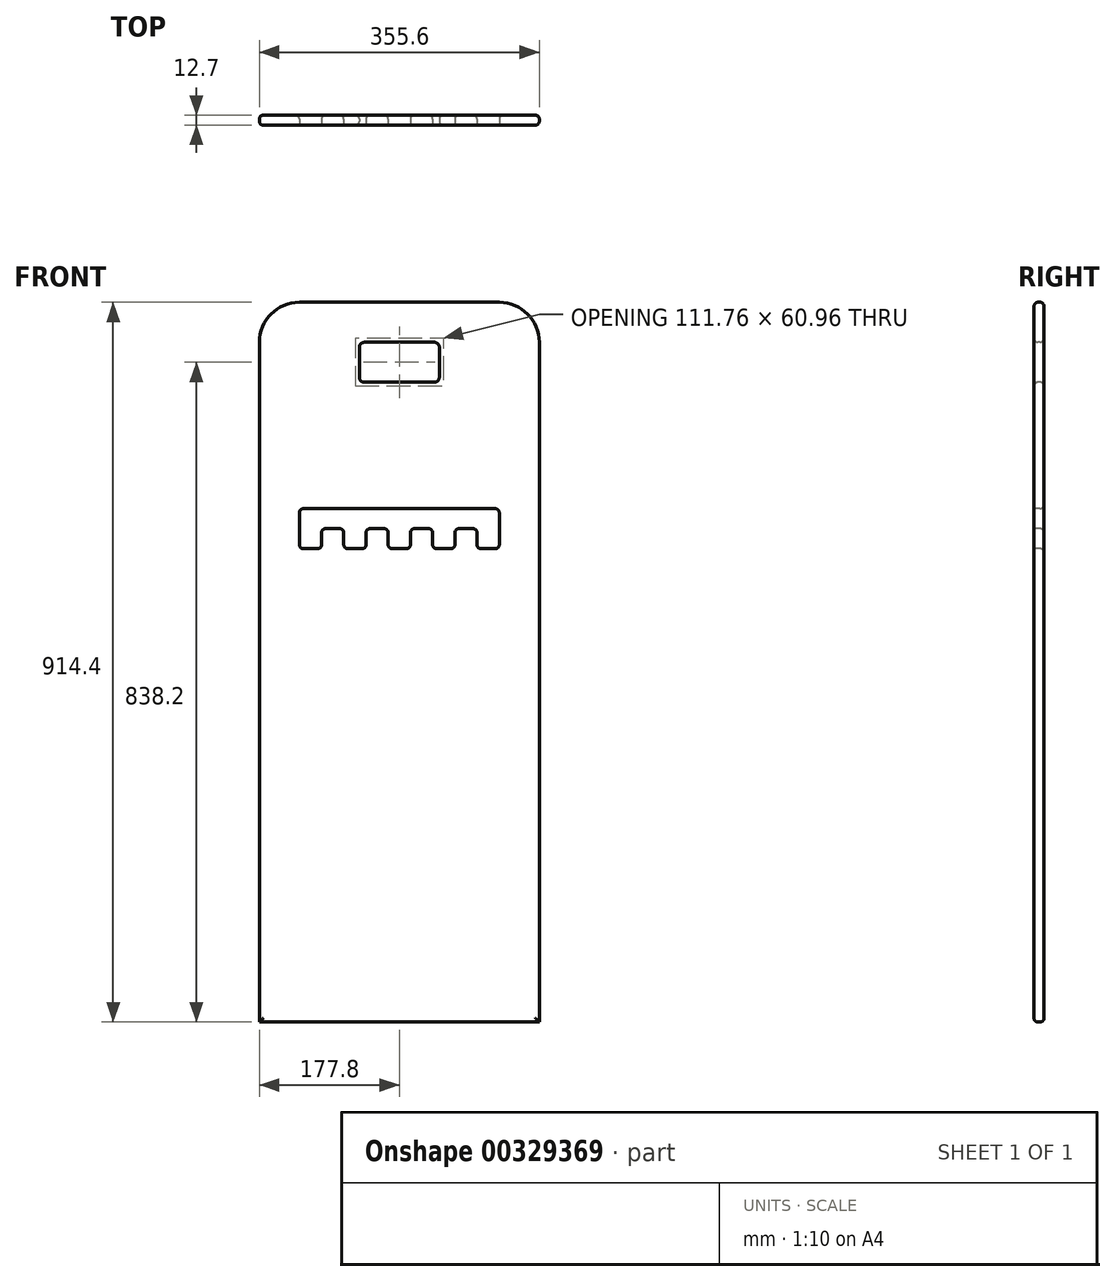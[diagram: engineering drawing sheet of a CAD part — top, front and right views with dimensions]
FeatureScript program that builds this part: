
annotation { "Feature Type Name" : "Feature", "Feature Type Description" : "" }
export const myFeature = defineFeature(function(context is Context, id is Id, definition is map)
    precondition{}
    {
        {
            var Q0;
            Q0=qCreatedBy(makeId("Front.planeOp"),FACE);
            var sketch = newSketch(context, id + "F0", { "sketchPlane" : qUnion([Q0])});
            skLineSegment(sketch, "E0.bottom", {"start": v(127, 457.2) * mm, "end": v(-127, 457.2) * mm});
            skLineSegment(sketch, "E0.top", {"start": v(177.8, -457.2) * mm, "end": v(-177.8, -457.2) * mm});
            skLineSegment(sketch, "E0.left", {"start": v(177.8, 406.4) * mm, "end": v(177.8, -457.2) * mm});
            skLineSegment(sketch, "E0.right", {"start": v(-177.8, 406.4) * mm, "end": v(-177.8, -457.2) * mm});
            skPoint(sketch, "E0.middle", {"position": v(0, 0) * mm});
            skPoint(sketch, "E1.visualSharp", {"position": v(-177.8, 457.2) * mm});
            skArc(sketch, "E1.filletArc", {"start": v(-127, 457.2) * mm, "mid": v(-162.92, 442.32) * mm, "end": v(-177.8, 406.4) * mm});
            skPoint(sketch, "E2.visualSharp", {"position": v(177.8, 457.2) * mm});
            skArc(sketch, "E2.filletArc", {"start": v(177.8, 406.4) * mm, "mid": v(162.92, 442.32) * mm, "end": v(127, 457.2) * mm});
            skSolve(sketch);
        }
        {
            var Q0;
            Q0 = qSketchRegion(id + "F0", true);
            extrude(context, id + "F1", {"entities" : qUnion([Q0]), "depth" : 12.7 * mm});
        }
        {
            var Q0;
            Q0=makeQuery(id+"F1.opExtrude","CAP_FACE",FACE,{"disambiguationData":[OSD([sQuery(id+"F0.wireOp",EDGE,"E0.bottom"),sQuery(id+"F0.wireOp",EDGE,"E0.top"),sQuery(id+"F0.wireOp",EDGE,"E0.left"),sQuery(id+"F0.wireOp",EDGE,"E0.right")])],"isStart":false});
            var sketch = newSketch(context, id + "F2", { "sketchPlane" : qUnion([Q0])});
            skLineSegment(sketch, "E3", {"start": v(0, 457.2) * mm, "end": v(127, 457.2) * mm, "construction": true});
            skLineSegment(sketch, "E4", {"start": v(0, 457.2) * mm, "end": v(0, 406.4) * mm, "construction": true});
            skLineSegment(sketch, "E5", {"start": v(0, 406.4) * mm, "end": v(-44.45, 406.4) * mm});
            skLineSegment(sketch, "E6", {"start": v(-50.8, 400.05) * mm, "end": v(-50.8, 361.95) * mm});
            skLineSegment(sketch, "E7", {"start": v(-44.45, 355.6) * mm, "end": v(44.45, 355.6) * mm});
            skLineSegment(sketch, "E8", {"start": v(50.8, 361.95) * mm, "end": v(50.8, 400.05) * mm});
            skLineSegment(sketch, "E9", {"start": v(44.45, 406.4) * mm, "end": v(0, 406.4) * mm});
            skPoint(sketch, "E10.visualSharp", {"position": v(-50.8, 406.4) * mm});
            skArc(sketch, "E10.filletArc", {"start": v(-44.45, 406.4) * mm, "mid": v(-48.94, 404.54) * mm, "end": v(-50.8, 400.05) * mm});
            skPoint(sketch, "E11.visualSharp", {"position": v(-50.8, 355.6) * mm});
            skArc(sketch, "E11.filletArc", {"start": v(-50.8, 361.95) * mm, "mid": v(-48.94, 357.46) * mm, "end": v(-44.45, 355.6) * mm});
            skPoint(sketch, "E12.visualSharp", {"position": v(50.8, 355.6) * mm});
            skArc(sketch, "E12.filletArc", {"start": v(44.45, 355.6) * mm, "mid": v(48.94, 357.46) * mm, "end": v(50.8, 361.95) * mm});
            skPoint(sketch, "E13.visualSharp", {"position": v(50.8, 406.4) * mm});
            skArc(sketch, "E13.filletArc", {"start": v(50.8, 400.05) * mm, "mid": v(48.94, 404.54) * mm, "end": v(44.45, 406.4) * mm});
            skSolve(sketch);
        }
        {
            var Q0;
            Q0=makeQuery(id+"F2.imprint","IMPRINT",FACE,{"disambiguationData":[TD([[makeQuery(id+"F2.imprint","IMPRINT",EDGE,{"derivedFrom":sQuery(id+"F2.wireOp",EDGE,"E5")}),1.0]])]});
            extrude(context, id + "F3", {"entities" : qUnion([Q0]), "operationType" : NewBodyOperationType.REMOVE, "oppositeDirection" : true, "depth" : 25.4 * mm});
        }
        {
            var Q0;
            Q0=makeQuery(id+"F1.opExtrude","CAP_FACE",FACE,{"disambiguationData":[OSD([sQuery(id+"F0.wireOp",EDGE,"E0.bottom"),sQuery(id+"F0.wireOp",EDGE,"E0.top"),sQuery(id+"F0.wireOp",EDGE,"E0.left"),sQuery(id+"F0.wireOp",EDGE,"E0.right"),sQuery(id+"F0.wireOp",EDGE,"E1.filletArc"),sQuery(id+"F0.wireOp",EDGE,"E2.filletArc")])],"isStart":false});
            fillet(context, id + "F4", {"entities" : qUnion([Q0]), "radius" : 5.08 * mm, "tangentPropagation" : true, "allowEdgeOverflow" : false});
        }
        {
            var Q0;
            Q0=makeQuery(id+"F1.opExtrude","CAP_FACE",FACE,{"disambiguationData":[OSD([sQuery(id+"F0.wireOp",EDGE,"E0.bottom"),sQuery(id+"F0.wireOp",EDGE,"E0.top"),sQuery(id+"F0.wireOp",EDGE,"E0.left"),sQuery(id+"F0.wireOp",EDGE,"E0.right"),sQuery(id+"F0.wireOp",EDGE,"E1.filletArc"),sQuery(id+"F0.wireOp",EDGE,"E2.filletArc")])],"isStart":true});
            fillet(context, id + "F5", {"entities" : qUnion([Q0]), "radius" : 5.08 * mm, "tangentPropagation" : true, "allowEdgeOverflow" : false});
        }
        {
            var Q0;
            Q0=makeQuery(id+"F1.opExtrude","CAP_FACE",FACE,{"disambiguationData":[OSD([sQuery(id+"F0.wireOp",EDGE,"E0.bottom"),sQuery(id+"F0.wireOp",EDGE,"E0.top"),sQuery(id+"F0.wireOp",EDGE,"E0.left"),sQuery(id+"F0.wireOp",EDGE,"E0.right"),sQuery(id+"F0.wireOp",EDGE,"E1.filletArc"),sQuery(id+"F0.wireOp",EDGE,"E2.filletArc")])],"isStart":false});
            var sketch = newSketch(context, id + "F6", { "sketchPlane" : qUnion([Q0])});
            skLineSegment(sketch, "E14", {"start": v(0, 452.12) * mm, "end": v(0, 194.94) * mm, "construction": true});
            skPoint(sketch, "E14.endSnap0", {"position": v(0, 452.12) * mm});
            skLineSegment(sketch, "E15", {"start": v(0, 194.94) * mm, "end": v(-127, 194.94) * mm});
            skLineSegment(sketch, "E16", {"start": v(-127, 194.94) * mm, "end": v(-127, 144.14) * mm});
            skLineSegment(sketch, "E17", {"start": v(-127, 144.14) * mm, "end": v(127, 144.14) * mm});
            skLineSegment(sketch, "E18", {"start": v(127, 144.14) * mm, "end": v(127, 194.94) * mm});
            skLineSegment(sketch, "E19", {"start": v(127, 194.94) * mm, "end": v(0, 194.94) * mm});
            skLineSegment(sketch, "E20", {"start": v(-127, 144.14) * mm, "end": v(-98.78, 144.14) * mm, "construction": true});
            skLineSegment(sketch, "E21", {"start": v(-98.78, 144.14) * mm, "end": v(-70.56, 144.14) * mm, "construction": true});
            skLineSegment(sketch, "E22", {"start": v(-70.56, 144.14) * mm, "end": v(-42.33, 144.14) * mm, "construction": true});
            skLineSegment(sketch, "E23", {"start": v(-42.33, 144.14) * mm, "end": v(-14.11, 144.14) * mm, "construction": true});
            skLineSegment(sketch, "E24", {"start": v(-14.11, 144.14) * mm, "end": v(14.11, 144.14) * mm, "construction": true});
            skLineSegment(sketch, "E25", {"start": v(14.11, 144.14) * mm, "end": v(42.33, 144.14) * mm, "construction": true});
            skLineSegment(sketch, "E26", {"start": v(42.33, 144.14) * mm, "end": v(70.56, 144.14) * mm, "construction": true});
            skLineSegment(sketch, "E27", {"start": v(70.56, 144.14) * mm, "end": v(98.78, 144.14) * mm, "construction": true});
            skLineSegment(sketch, "E28", {"start": v(98.78, 144.14) * mm, "end": v(98.78, 169.54) * mm});
            skPoint(sketch, "E28.endSnap0", {"position": v(127, 169.54) * mm});
            skLineSegment(sketch, "E29", {"start": v(98.78, 169.54) * mm, "end": v(70.56, 169.54) * mm});
            skLineSegment(sketch, "E30", {"start": v(70.56, 169.54) * mm, "end": v(70.56, 144.14) * mm});
            skLineSegment(sketch, "E31", {"start": v(-98.78, 144.14) * mm, "end": v(-98.78, 169.54) * mm});
            skLineSegment(sketch, "E32", {"start": v(-98.78, 169.54) * mm, "end": v(-70.56, 169.54) * mm});
            skLineSegment(sketch, "E33", {"start": v(-70.56, 169.54) * mm, "end": v(-70.56, 144.14) * mm});
            skLineSegment(sketch, "E34", {"start": v(-42.33, 144.14) * mm, "end": v(-42.33, 169.54) * mm});
            skLineSegment(sketch, "E35", {"start": v(-42.33, 169.54) * mm, "end": v(-14.11, 169.54) * mm});
            skLineSegment(sketch, "E36", {"start": v(-14.11, 169.54) * mm, "end": v(-14.11, 144.14) * mm});
            skLineSegment(sketch, "E37", {"start": v(14.11, 144.14) * mm, "end": v(14.11, 169.54) * mm});
            skLineSegment(sketch, "E38", {"start": v(14.11, 169.54) * mm, "end": v(42.33, 169.54) * mm});
            skLineSegment(sketch, "E39", {"start": v(42.33, 144.14) * mm, "end": v(42.33, 169.54) * mm});
            skSolve(sketch);
        }
        {
            var Q0;
            Q0=makeQuery(id+"F6.imprint","IMPRINT",FACE,{"disambiguationData":[TD([[makeQuery(id+"F6.imprint","IMPRINT",EDGE,{"derivedFrom":sQuery(id+"F6.wireOp",EDGE,"E15")}),1.0]])]});
            extrude(context, id + "F7", {"entities" : qUnion([Q0]), "operationType" : NewBodyOperationType.REMOVE, "oppositeDirection" : true, "depth" : 25.4 * mm});
        }
        {
            var Q0;
            Q0=makeQuery(id+"F7.boolean.opBoolean","COPY",EDGE,{"derivedFrom":makeQuery(id+"F7.opExtrude","CAP_EDGE",EDGE,{"disambiguationData":[OSD([sQuery(id+"F6.wireOp",EDGE,"E31")])],"isStart":true})});
            var Q1;
            Q1=makeQuery(id+"F7.boolean.opBoolean","COPY",EDGE,{"derivedFrom":makeQuery(id+"F7.opExtrude","CAP_EDGE",EDGE,{"disambiguationData":[OSD([sQuery(id+"F6.wireOp",EDGE,"E32")])],"isStart":true})});
            var Q2;
            Q2=makeQuery(id+"F7.boolean.opBoolean","COPY",EDGE,{"derivedFrom":makeQuery(id+"F7.opExtrude","CAP_EDGE",EDGE,{"disambiguationData":[OSD([sQuery(id+"F6.wireOp",EDGE,"E33")])],"isStart":true})});
            var Q3;
            Q3=makeQuery(id+"F7.boolean.opBoolean","COPY",EDGE,{"derivedFrom":makeQuery(id+"F7.opExtrude","CAP_EDGE",EDGE,{"disambiguationData":[OSD([sQuery(id+"F6.wireOp",EDGE,"E34")])],"isStart":true})});
            var Q4;
            Q4=makeQuery(id+"F7.boolean.opBoolean","COPY",EDGE,{"derivedFrom":makeQuery(id+"F7.opExtrude","CAP_EDGE",EDGE,{"disambiguationData":[OSD([sQuery(id+"F6.wireOp",EDGE,"E35")])],"isStart":true})});
            var Q5;
            Q5=makeQuery(id+"F7.boolean.opBoolean","COPY",EDGE,{"derivedFrom":makeQuery(id+"F7.opExtrude","CAP_EDGE",EDGE,{"disambiguationData":[OSD([sQuery(id+"F6.wireOp",EDGE,"E15"),sQuery(id+"F6.wireOp",EDGE,"E19")])],"isStart":true})});
            var Q6;
            Q6=makeQuery(id+"F7.boolean.opBoolean","COPY",EDGE,{"derivedFrom":makeQuery(id+"F7.opExtrude","CAP_EDGE",EDGE,{"disambiguationData":[OSD([sQuery(id+"F6.wireOp",EDGE,"E36")])],"isStart":true})});
            var Q7;
            Q7=makeQuery(id+"F7.boolean.opBoolean","COPY",EDGE,{"derivedFrom":makeQuery(id+"F7.opExtrude","CAP_EDGE",EDGE,{"disambiguationData":[OSD([sQuery(id+"F6.wireOp",EDGE,"E16")])],"isStart":true})});
            var Q8;
            Q8=makeQuery(id+"F7.boolean.opBoolean","COPY",EDGE,{"derivedFrom":makeQuery(id+"F7.opExtrude","CAP_EDGE",EDGE,{"disambiguationData":[OSD([sQuery(id+"F6.wireOp",EDGE,"E37")])],"isStart":true})});
            var Q9;
            {var subQ0=sQuery(id+"F6.wireOp",EDGE,"E17");Q9=makeQuery(id+"F7.boolean.opBoolean","COPY",EDGE,{"derivedFrom":makeQuery(id+"F7.opExtrude","CAP_EDGE",EDGE,{"disambiguationData":[OSD([subQ0]),TDD([makeQuery(id+"F6.imprint","IMPRINT",EDGE,{"disambiguationData":[TD([[makeQuery(id+"F6.imprint","INTERSECT",VERTEX,{"derivedFrom":[sQuery(id+"F6.wireOp",EDGE,"E16"),subQ0]}),-1.0]])],"derivedFrom":subQ0})])],"isStart":true})});}
            var Q10;
            Q10=makeQuery(id+"F7.boolean.opBoolean","COPY",EDGE,{"derivedFrom":makeQuery(id+"F7.opExtrude","CAP_EDGE",EDGE,{"disambiguationData":[OSD([sQuery(id+"F6.wireOp",EDGE,"E38")])],"isStart":true})});
            var Q11;
            {var subQ0=sQuery(id+"F6.wireOp",EDGE,"E17");Q11=makeQuery(id+"F7.boolean.opBoolean","COPY",EDGE,{"derivedFrom":makeQuery(id+"F7.opExtrude","CAP_EDGE",EDGE,{"disambiguationData":[OSD([subQ0]),TDD([makeQuery(id+"F6.imprint","IMPRINT",EDGE,{"disambiguationData":[TD([[makeQuery(id+"F6.imprint","INTERSECT",VERTEX,{"derivedFrom":[subQ0,sQuery(id+"F6.wireOp",EDGE,"E33")]}),-1.0]])],"derivedFrom":subQ0})])],"isStart":true})});}
            var Q12;
            {var subQ0=sQuery(id+"F6.wireOp",EDGE,"E17");Q12=makeQuery(id+"F7.boolean.opBoolean","COPY",EDGE,{"derivedFrom":makeQuery(id+"F7.opExtrude","CAP_EDGE",EDGE,{"disambiguationData":[OSD([subQ0]),TDD([makeQuery(id+"F6.imprint","IMPRINT",EDGE,{"disambiguationData":[TD([[makeQuery(id+"F6.imprint","INTERSECT",VERTEX,{"derivedFrom":[subQ0,sQuery(id+"F6.wireOp",EDGE,"E36")]}),-1.0]])],"derivedFrom":subQ0})])],"isStart":true})});}
            var Q13;
            {var subQ0=sQuery(id+"F6.wireOp",EDGE,"E17");Q13=makeQuery(id+"F7.boolean.opBoolean","COPY",EDGE,{"derivedFrom":makeQuery(id+"F7.opExtrude","CAP_EDGE",EDGE,{"disambiguationData":[OSD([subQ0]),TDD([makeQuery(id+"F6.imprint","IMPRINT",EDGE,{"disambiguationData":[TD([[makeQuery(id+"F6.imprint","INTERSECT",VERTEX,{"derivedFrom":[subQ0,sQuery(id+"F6.wireOp",EDGE,"E30")]}),1.0]])],"derivedFrom":subQ0})])],"isStart":true})});}
            var Q14;
            {var subQ0=sQuery(id+"F6.wireOp",EDGE,"E17");Q14=makeQuery(id+"F7.boolean.opBoolean","COPY",EDGE,{"derivedFrom":makeQuery(id+"F7.opExtrude","CAP_EDGE",EDGE,{"disambiguationData":[OSD([subQ0]),TDD([makeQuery(id+"F6.imprint","IMPRINT",EDGE,{"disambiguationData":[TD([[makeQuery(id+"F6.imprint","INTERSECT",VERTEX,{"derivedFrom":[subQ0,sQuery(id+"F6.wireOp",EDGE,"E18")]}),1.0]])],"derivedFrom":subQ0})])],"isStart":true})});}
            var Q15;
            Q15=makeQuery(id+"F7.boolean.opBoolean","COPY",EDGE,{"derivedFrom":makeQuery(id+"F7.opExtrude","CAP_EDGE",EDGE,{"disambiguationData":[OSD([sQuery(id+"F6.wireOp",EDGE,"E18")])],"isStart":true})});
            var Q16;
            Q16=makeQuery(id+"F7.boolean.opBoolean","COPY",EDGE,{"derivedFrom":makeQuery(id+"F7.opExtrude","SWEPT_EDGE",EDGE,{"disambiguationData":[OSD([sQuery(id+"F6.wireOp",EDGE,"E34"),sQuery(id+"F6.wireOp",EDGE,"E35")])]})});
            var Q17;
            Q17=makeQuery(id+"F7.boolean.opBoolean","COPY",EDGE,{"derivedFrom":makeQuery(id+"F7.opExtrude","SWEPT_EDGE",EDGE,{"disambiguationData":[OSD([sQuery(id+"F6.wireOp",EDGE,"E15"),sQuery(id+"F6.wireOp",EDGE,"E16")])]})});
            var Q18;
            Q18=makeQuery(id+"F7.boolean.opBoolean","COPY",EDGE,{"derivedFrom":makeQuery(id+"F7.opExtrude","SWEPT_EDGE",EDGE,{"disambiguationData":[OSD([sQuery(id+"F6.wireOp",EDGE,"E16"),sQuery(id+"F6.wireOp",EDGE,"E17")])]})});
            var Q19;
            Q19=makeQuery(id+"F7.boolean.opBoolean","COPY",EDGE,{"derivedFrom":makeQuery(id+"F7.opExtrude","SWEPT_EDGE",EDGE,{"disambiguationData":[OSD([sQuery(id+"F6.wireOp",EDGE,"E17"),sQuery(id+"F6.wireOp",EDGE,"E28")])]})});
            var Q20;
            Q20=makeQuery(id+"F7.boolean.opBoolean","COPY",EDGE,{"derivedFrom":makeQuery(id+"F7.opExtrude","SWEPT_EDGE",EDGE,{"disambiguationData":[OSD([sQuery(id+"F6.wireOp",EDGE,"E28"),sQuery(id+"F6.wireOp",EDGE,"E29")])]})});
            var Q21;
            Q21=makeQuery(id+"F7.boolean.opBoolean","COPY",EDGE,{"derivedFrom":makeQuery(id+"F7.opExtrude","SWEPT_EDGE",EDGE,{"disambiguationData":[OSD([sQuery(id+"F6.wireOp",EDGE,"E29"),sQuery(id+"F6.wireOp",EDGE,"E30")])]})});
            var Q22;
            Q22=makeQuery(id+"F7.boolean.opBoolean","COPY",EDGE,{"derivedFrom":makeQuery(id+"F7.opExtrude","SWEPT_EDGE",EDGE,{"disambiguationData":[OSD([sQuery(id+"F6.wireOp",EDGE,"E17"),sQuery(id+"F6.wireOp",EDGE,"E30")])]})});
            var Q23;
            Q23=makeQuery(id+"F7.boolean.opBoolean","COPY",EDGE,{"derivedFrom":makeQuery(id+"F7.opExtrude","SWEPT_EDGE",EDGE,{"disambiguationData":[OSD([sQuery(id+"F6.wireOp",EDGE,"E17"),sQuery(id+"F6.wireOp",EDGE,"E31")])]})});
            var Q24;
            Q24=makeQuery(id+"F7.boolean.opBoolean","COPY",EDGE,{"derivedFrom":makeQuery(id+"F7.opExtrude","CAP_EDGE",EDGE,{"disambiguationData":[OSD([sQuery(id+"F6.wireOp",EDGE,"E29")])],"isStart":true})});
            var Q25;
            {var subQ0=sQuery(id+"F6.wireOp",EDGE,"E17");Q25=makeQuery(id+"F7.boolean.opBoolean","INTERSECT",EDGE,{"derivedFrom":[makeQuery(id+"F1.opExtrude","CAP_FACE",FACE,{"disambiguationData":[OSD([sQuery(id+"F0.wireOp",EDGE,"E0.bottom"),sQuery(id+"F0.wireOp",EDGE,"E0.top"),sQuery(id+"F0.wireOp",EDGE,"E0.left"),sQuery(id+"F0.wireOp",EDGE,"E0.right"),sQuery(id+"F0.wireOp",EDGE,"E1.filletArc"),sQuery(id+"F0.wireOp",EDGE,"E2.filletArc")])],"isStart":true}),makeQuery(id+"F7.opExtrude","SWEPT_FACE",FACE,{"disambiguationData":[OSD([subQ0]),TDD([makeQuery(id+"F6.imprint","IMPRINT",EDGE,{"disambiguationData":[TD([[makeQuery(id+"F6.imprint","INTERSECT",VERTEX,{"derivedFrom":[subQ0,sQuery(id+"F6.wireOp",EDGE,"E30")]}),1.0]])],"derivedFrom":subQ0})])]})]});}
            var Q26;
            Q26=makeQuery(id+"F7.boolean.opBoolean","COPY",EDGE,{"derivedFrom":makeQuery(id+"F7.opExtrude","CAP_EDGE",EDGE,{"disambiguationData":[OSD([sQuery(id+"F6.wireOp",EDGE,"E30")])],"isStart":true})});
            var Q27;
            {var subQ0=sQuery(id+"F6.wireOp",EDGE,"E17");Q27=makeQuery(id+"F7.boolean.opBoolean","INTERSECT",EDGE,{"derivedFrom":[makeQuery(id+"F1.opExtrude","CAP_FACE",FACE,{"disambiguationData":[OSD([sQuery(id+"F0.wireOp",EDGE,"E0.bottom"),sQuery(id+"F0.wireOp",EDGE,"E0.top"),sQuery(id+"F0.wireOp",EDGE,"E0.left"),sQuery(id+"F0.wireOp",EDGE,"E0.right"),sQuery(id+"F0.wireOp",EDGE,"E1.filletArc"),sQuery(id+"F0.wireOp",EDGE,"E2.filletArc")])],"isStart":true}),makeQuery(id+"F7.opExtrude","SWEPT_FACE",FACE,{"disambiguationData":[OSD([subQ0]),TDD([makeQuery(id+"F6.imprint","IMPRINT",EDGE,{"disambiguationData":[TD([[makeQuery(id+"F6.imprint","INTERSECT",VERTEX,{"derivedFrom":[subQ0,sQuery(id+"F6.wireOp",EDGE,"E18")]}),1.0]])],"derivedFrom":subQ0})])]})]});}
            var Q28;
            Q28=makeQuery(id+"F7.boolean.opBoolean","COPY",EDGE,{"derivedFrom":makeQuery(id+"F7.opExtrude","SWEPT_EDGE",EDGE,{"disambiguationData":[OSD([sQuery(id+"F6.wireOp",EDGE,"E17"),sQuery(id+"F6.wireOp",EDGE,"E37")])]})});
            var Q29;
            Q29=makeQuery(id+"F7.boolean.opBoolean","COPY",EDGE,{"derivedFrom":makeQuery(id+"F7.opExtrude","SWEPT_EDGE",EDGE,{"disambiguationData":[OSD([sQuery(id+"F6.wireOp",EDGE,"E17"),sQuery(id+"F6.wireOp",EDGE,"E39")])]})});
            var Q30;
            Q30=makeQuery(id+"F7.boolean.opBoolean","INTERSECT",EDGE,{"derivedFrom":[makeQuery(id+"F1.opExtrude","CAP_FACE",FACE,{"disambiguationData":[OSD([sQuery(id+"F0.wireOp",EDGE,"E0.bottom"),sQuery(id+"F0.wireOp",EDGE,"E0.top"),sQuery(id+"F0.wireOp",EDGE,"E0.left"),sQuery(id+"F0.wireOp",EDGE,"E0.right"),sQuery(id+"F0.wireOp",EDGE,"E1.filletArc"),sQuery(id+"F0.wireOp",EDGE,"E2.filletArc")])],"isStart":true}),makeQuery(id+"F7.opExtrude","SWEPT_FACE",FACE,{"disambiguationData":[OSD([sQuery(id+"F6.wireOp",EDGE,"E31")])]})]});
            var Q31;
            Q31=makeQuery(id+"F7.boolean.opBoolean","INTERSECT",EDGE,{"derivedFrom":[makeQuery(id+"F1.opExtrude","CAP_FACE",FACE,{"disambiguationData":[OSD([sQuery(id+"F0.wireOp",EDGE,"E0.bottom"),sQuery(id+"F0.wireOp",EDGE,"E0.top"),sQuery(id+"F0.wireOp",EDGE,"E0.left"),sQuery(id+"F0.wireOp",EDGE,"E0.right"),sQuery(id+"F0.wireOp",EDGE,"E1.filletArc"),sQuery(id+"F0.wireOp",EDGE,"E2.filletArc")])],"isStart":true}),makeQuery(id+"F7.opExtrude","SWEPT_FACE",FACE,{"disambiguationData":[OSD([sQuery(id+"F6.wireOp",EDGE,"E33")])]})]});
            var Q32;
            Q32=makeQuery(id+"F7.boolean.opBoolean","INTERSECT",EDGE,{"derivedFrom":[makeQuery(id+"F1.opExtrude","CAP_FACE",FACE,{"disambiguationData":[OSD([sQuery(id+"F0.wireOp",EDGE,"E0.bottom"),sQuery(id+"F0.wireOp",EDGE,"E0.top"),sQuery(id+"F0.wireOp",EDGE,"E0.left"),sQuery(id+"F0.wireOp",EDGE,"E0.right"),sQuery(id+"F0.wireOp",EDGE,"E1.filletArc"),sQuery(id+"F0.wireOp",EDGE,"E2.filletArc")])],"isStart":true}),makeQuery(id+"F7.opExtrude","SWEPT_FACE",FACE,{"disambiguationData":[OSD([sQuery(id+"F6.wireOp",EDGE,"E34")])]})]});
            var Q33;
            Q33=makeQuery(id+"F7.boolean.opBoolean","COPY",EDGE,{"derivedFrom":makeQuery(id+"F7.opExtrude","CAP_EDGE",EDGE,{"disambiguationData":[OSD([sQuery(id+"F6.wireOp",EDGE,"E39")])],"isStart":true})});
            var Q34;
            Q34=makeQuery(id+"F7.boolean.opBoolean","INTERSECT",EDGE,{"derivedFrom":[makeQuery(id+"F1.opExtrude","CAP_FACE",FACE,{"disambiguationData":[OSD([sQuery(id+"F0.wireOp",EDGE,"E0.bottom"),sQuery(id+"F0.wireOp",EDGE,"E0.top"),sQuery(id+"F0.wireOp",EDGE,"E0.left"),sQuery(id+"F0.wireOp",EDGE,"E0.right"),sQuery(id+"F0.wireOp",EDGE,"E1.filletArc"),sQuery(id+"F0.wireOp",EDGE,"E2.filletArc")])],"isStart":true}),makeQuery(id+"F7.opExtrude","SWEPT_FACE",FACE,{"disambiguationData":[OSD([sQuery(id+"F6.wireOp",EDGE,"E35")])]})]});
            var Q35;
            Q35=makeQuery(id+"F7.boolean.opBoolean","INTERSECT",EDGE,{"derivedFrom":[makeQuery(id+"F1.opExtrude","CAP_FACE",FACE,{"disambiguationData":[OSD([sQuery(id+"F0.wireOp",EDGE,"E0.bottom"),sQuery(id+"F0.wireOp",EDGE,"E0.top"),sQuery(id+"F0.wireOp",EDGE,"E0.left"),sQuery(id+"F0.wireOp",EDGE,"E0.right"),sQuery(id+"F0.wireOp",EDGE,"E1.filletArc"),sQuery(id+"F0.wireOp",EDGE,"E2.filletArc")])],"isStart":true}),makeQuery(id+"F7.opExtrude","SWEPT_FACE",FACE,{"disambiguationData":[OSD([sQuery(id+"F6.wireOp",EDGE,"E15"),sQuery(id+"F6.wireOp",EDGE,"E19")])]})]});
            var Q36;
            Q36=makeQuery(id+"F7.boolean.opBoolean","INTERSECT",EDGE,{"derivedFrom":[makeQuery(id+"F1.opExtrude","CAP_FACE",FACE,{"disambiguationData":[OSD([sQuery(id+"F0.wireOp",EDGE,"E0.bottom"),sQuery(id+"F0.wireOp",EDGE,"E0.top"),sQuery(id+"F0.wireOp",EDGE,"E0.left"),sQuery(id+"F0.wireOp",EDGE,"E0.right"),sQuery(id+"F0.wireOp",EDGE,"E1.filletArc"),sQuery(id+"F0.wireOp",EDGE,"E2.filletArc")])],"isStart":true}),makeQuery(id+"F7.opExtrude","SWEPT_FACE",FACE,{"disambiguationData":[OSD([sQuery(id+"F6.wireOp",EDGE,"E16")])]})]});
            var Q37;
            Q37=makeQuery(id+"F7.boolean.opBoolean","INTERSECT",EDGE,{"derivedFrom":[makeQuery(id+"F1.opExtrude","CAP_FACE",FACE,{"disambiguationData":[OSD([sQuery(id+"F0.wireOp",EDGE,"E0.bottom"),sQuery(id+"F0.wireOp",EDGE,"E0.top"),sQuery(id+"F0.wireOp",EDGE,"E0.left"),sQuery(id+"F0.wireOp",EDGE,"E0.right"),sQuery(id+"F0.wireOp",EDGE,"E1.filletArc"),sQuery(id+"F0.wireOp",EDGE,"E2.filletArc")])],"isStart":true}),makeQuery(id+"F7.opExtrude","SWEPT_FACE",FACE,{"disambiguationData":[OSD([sQuery(id+"F6.wireOp",EDGE,"E37")])]})]});
            var Q38;
            {var subQ0=sQuery(id+"F6.wireOp",EDGE,"E17");Q38=makeQuery(id+"F7.boolean.opBoolean","INTERSECT",EDGE,{"derivedFrom":[makeQuery(id+"F1.opExtrude","CAP_FACE",FACE,{"disambiguationData":[OSD([sQuery(id+"F0.wireOp",EDGE,"E0.bottom"),sQuery(id+"F0.wireOp",EDGE,"E0.top"),sQuery(id+"F0.wireOp",EDGE,"E0.left"),sQuery(id+"F0.wireOp",EDGE,"E0.right"),sQuery(id+"F0.wireOp",EDGE,"E1.filletArc"),sQuery(id+"F0.wireOp",EDGE,"E2.filletArc")])],"isStart":true}),makeQuery(id+"F7.opExtrude","SWEPT_FACE",FACE,{"disambiguationData":[OSD([subQ0]),TDD([makeQuery(id+"F6.imprint","IMPRINT",EDGE,{"disambiguationData":[TD([[makeQuery(id+"F6.imprint","INTERSECT",VERTEX,{"derivedFrom":[sQuery(id+"F6.wireOp",EDGE,"E16"),subQ0]}),-1.0]])],"derivedFrom":subQ0})])]})]});}
            var Q39;
            Q39=makeQuery(id+"F7.boolean.opBoolean","COPY",EDGE,{"derivedFrom":makeQuery(id+"F7.opExtrude","CAP_EDGE",EDGE,{"disambiguationData":[OSD([sQuery(id+"F6.wireOp",EDGE,"E28")])],"isStart":true})});
            var Q40;
            {var subQ0=sQuery(id+"F6.wireOp",EDGE,"E17");Q40=makeQuery(id+"F7.boolean.opBoolean","INTERSECT",EDGE,{"derivedFrom":[makeQuery(id+"F1.opExtrude","CAP_FACE",FACE,{"disambiguationData":[OSD([sQuery(id+"F0.wireOp",EDGE,"E0.bottom"),sQuery(id+"F0.wireOp",EDGE,"E0.top"),sQuery(id+"F0.wireOp",EDGE,"E0.left"),sQuery(id+"F0.wireOp",EDGE,"E0.right"),sQuery(id+"F0.wireOp",EDGE,"E1.filletArc"),sQuery(id+"F0.wireOp",EDGE,"E2.filletArc")])],"isStart":true}),makeQuery(id+"F7.opExtrude","SWEPT_FACE",FACE,{"disambiguationData":[OSD([subQ0]),TDD([makeQuery(id+"F6.imprint","IMPRINT",EDGE,{"disambiguationData":[TD([[makeQuery(id+"F6.imprint","INTERSECT",VERTEX,{"derivedFrom":[subQ0,sQuery(id+"F6.wireOp",EDGE,"E36")]}),-1.0]])],"derivedFrom":subQ0})])]})]});}
            var Q41;
            Q41=makeQuery(id+"F7.boolean.opBoolean","COPY",EDGE,{"derivedFrom":makeQuery(id+"F7.opExtrude","SWEPT_EDGE",EDGE,{"disambiguationData":[OSD([sQuery(id+"F6.wireOp",EDGE,"E35"),sQuery(id+"F6.wireOp",EDGE,"E36")])]})});
            var Q42;
            Q42=makeQuery(id+"F7.boolean.opBoolean","COPY",EDGE,{"derivedFrom":makeQuery(id+"F7.opExtrude","SWEPT_EDGE",EDGE,{"disambiguationData":[OSD([sQuery(id+"F6.wireOp",EDGE,"E17"),sQuery(id+"F6.wireOp",EDGE,"E36")])]})});
            var Q43;
            Q43=makeQuery(id+"F7.boolean.opBoolean","COPY",EDGE,{"derivedFrom":makeQuery(id+"F7.opExtrude","SWEPT_EDGE",EDGE,{"disambiguationData":[OSD([sQuery(id+"F6.wireOp",EDGE,"E17"),sQuery(id+"F6.wireOp",EDGE,"E18")])]})});
            var Q44;
            Q44=makeQuery(id+"F7.boolean.opBoolean","COPY",EDGE,{"derivedFrom":makeQuery(id+"F7.opExtrude","SWEPT_EDGE",EDGE,{"disambiguationData":[OSD([sQuery(id+"F6.wireOp",EDGE,"E18"),sQuery(id+"F6.wireOp",EDGE,"E19")])]})});
            var Q45;
            Q45=makeQuery(id+"F7.boolean.opBoolean","COPY",EDGE,{"derivedFrom":makeQuery(id+"F7.opExtrude","SWEPT_EDGE",EDGE,{"disambiguationData":[OSD([sQuery(id+"F6.wireOp",EDGE,"E31"),sQuery(id+"F6.wireOp",EDGE,"E32")])]})});
            var Q46;
            Q46=makeQuery(id+"F7.boolean.opBoolean","COPY",EDGE,{"derivedFrom":makeQuery(id+"F7.opExtrude","SWEPT_EDGE",EDGE,{"disambiguationData":[OSD([sQuery(id+"F6.wireOp",EDGE,"E32"),sQuery(id+"F6.wireOp",EDGE,"E33")])]})});
            var Q47;
            Q47=makeQuery(id+"F7.boolean.opBoolean","COPY",EDGE,{"derivedFrom":makeQuery(id+"F7.opExtrude","SWEPT_EDGE",EDGE,{"disambiguationData":[OSD([sQuery(id+"F6.wireOp",EDGE,"E17"),sQuery(id+"F6.wireOp",EDGE,"E33")])]})});
            var Q48;
            Q48=makeQuery(id+"F7.boolean.opBoolean","COPY",EDGE,{"derivedFrom":makeQuery(id+"F7.opExtrude","SWEPT_EDGE",EDGE,{"disambiguationData":[OSD([sQuery(id+"F6.wireOp",EDGE,"E17"),sQuery(id+"F6.wireOp",EDGE,"E34")])]})});
            var Q49;
            Q49=makeQuery(id+"F7.boolean.opBoolean","INTERSECT",EDGE,{"derivedFrom":[makeQuery(id+"F1.opExtrude","CAP_FACE",FACE,{"disambiguationData":[OSD([sQuery(id+"F0.wireOp",EDGE,"E0.bottom"),sQuery(id+"F0.wireOp",EDGE,"E0.top"),sQuery(id+"F0.wireOp",EDGE,"E0.left"),sQuery(id+"F0.wireOp",EDGE,"E0.right"),sQuery(id+"F0.wireOp",EDGE,"E1.filletArc"),sQuery(id+"F0.wireOp",EDGE,"E2.filletArc")])],"isStart":true}),makeQuery(id+"F7.opExtrude","SWEPT_FACE",FACE,{"disambiguationData":[OSD([sQuery(id+"F6.wireOp",EDGE,"E18")])]})]});
            var Q50;
            Q50=makeQuery(id+"F7.boolean.opBoolean","INTERSECT",EDGE,{"derivedFrom":[makeQuery(id+"F1.opExtrude","CAP_FACE",FACE,{"disambiguationData":[OSD([sQuery(id+"F0.wireOp",EDGE,"E0.bottom"),sQuery(id+"F0.wireOp",EDGE,"E0.top"),sQuery(id+"F0.wireOp",EDGE,"E0.left"),sQuery(id+"F0.wireOp",EDGE,"E0.right"),sQuery(id+"F0.wireOp",EDGE,"E1.filletArc"),sQuery(id+"F0.wireOp",EDGE,"E2.filletArc")])],"isStart":true}),makeQuery(id+"F7.opExtrude","SWEPT_FACE",FACE,{"disambiguationData":[OSD([sQuery(id+"F6.wireOp",EDGE,"E28")])]})]});
            var Q51;
            Q51=makeQuery(id+"F7.boolean.opBoolean","COPY",EDGE,{"derivedFrom":makeQuery(id+"F7.opExtrude","SWEPT_EDGE",EDGE,{"disambiguationData":[OSD([sQuery(id+"F6.wireOp",EDGE,"E37"),sQuery(id+"F6.wireOp",EDGE,"E38")])]})});
            var Q52;
            Q52=makeQuery(id+"F7.boolean.opBoolean","INTERSECT",EDGE,{"derivedFrom":[makeQuery(id+"F1.opExtrude","CAP_FACE",FACE,{"disambiguationData":[OSD([sQuery(id+"F0.wireOp",EDGE,"E0.bottom"),sQuery(id+"F0.wireOp",EDGE,"E0.top"),sQuery(id+"F0.wireOp",EDGE,"E0.left"),sQuery(id+"F0.wireOp",EDGE,"E0.right"),sQuery(id+"F0.wireOp",EDGE,"E1.filletArc"),sQuery(id+"F0.wireOp",EDGE,"E2.filletArc")])],"isStart":true}),makeQuery(id+"F7.opExtrude","SWEPT_FACE",FACE,{"disambiguationData":[OSD([sQuery(id+"F6.wireOp",EDGE,"E29")])]})]});
            var Q53;
            Q53=makeQuery(id+"F7.boolean.opBoolean","COPY",EDGE,{"derivedFrom":makeQuery(id+"F7.opExtrude","SWEPT_EDGE",EDGE,{"disambiguationData":[OSD([sQuery(id+"F6.wireOp",EDGE,"E38"),sQuery(id+"F6.wireOp",EDGE,"E39")])]})});
            var Q54;
            Q54=makeQuery(id+"F7.boolean.opBoolean","INTERSECT",EDGE,{"derivedFrom":[makeQuery(id+"F1.opExtrude","CAP_FACE",FACE,{"disambiguationData":[OSD([sQuery(id+"F0.wireOp",EDGE,"E0.bottom"),sQuery(id+"F0.wireOp",EDGE,"E0.top"),sQuery(id+"F0.wireOp",EDGE,"E0.left"),sQuery(id+"F0.wireOp",EDGE,"E0.right"),sQuery(id+"F0.wireOp",EDGE,"E1.filletArc"),sQuery(id+"F0.wireOp",EDGE,"E2.filletArc")])],"isStart":true}),makeQuery(id+"F7.opExtrude","SWEPT_FACE",FACE,{"disambiguationData":[OSD([sQuery(id+"F6.wireOp",EDGE,"E30")])]})]});
            var Q55;
            Q55=makeQuery(id+"F7.boolean.opBoolean","INTERSECT",EDGE,{"derivedFrom":[makeQuery(id+"F1.opExtrude","CAP_FACE",FACE,{"disambiguationData":[OSD([sQuery(id+"F0.wireOp",EDGE,"E0.bottom"),sQuery(id+"F0.wireOp",EDGE,"E0.top"),sQuery(id+"F0.wireOp",EDGE,"E0.left"),sQuery(id+"F0.wireOp",EDGE,"E0.right"),sQuery(id+"F0.wireOp",EDGE,"E1.filletArc"),sQuery(id+"F0.wireOp",EDGE,"E2.filletArc")])],"isStart":true}),makeQuery(id+"F7.opExtrude","SWEPT_FACE",FACE,{"disambiguationData":[OSD([sQuery(id+"F6.wireOp",EDGE,"E32")])]})]});
            var Q56;
            Q56=makeQuery(id+"F7.boolean.opBoolean","INTERSECT",EDGE,{"derivedFrom":[makeQuery(id+"F1.opExtrude","CAP_FACE",FACE,{"disambiguationData":[OSD([sQuery(id+"F0.wireOp",EDGE,"E0.bottom"),sQuery(id+"F0.wireOp",EDGE,"E0.top"),sQuery(id+"F0.wireOp",EDGE,"E0.left"),sQuery(id+"F0.wireOp",EDGE,"E0.right"),sQuery(id+"F0.wireOp",EDGE,"E1.filletArc"),sQuery(id+"F0.wireOp",EDGE,"E2.filletArc")])],"isStart":true}),makeQuery(id+"F7.opExtrude","SWEPT_FACE",FACE,{"disambiguationData":[OSD([sQuery(id+"F6.wireOp",EDGE,"E36")])]})]});
            var Q57;
            Q57=makeQuery(id+"F7.boolean.opBoolean","INTERSECT",EDGE,{"derivedFrom":[makeQuery(id+"F1.opExtrude","CAP_FACE",FACE,{"disambiguationData":[OSD([sQuery(id+"F0.wireOp",EDGE,"E0.bottom"),sQuery(id+"F0.wireOp",EDGE,"E0.top"),sQuery(id+"F0.wireOp",EDGE,"E0.left"),sQuery(id+"F0.wireOp",EDGE,"E0.right"),sQuery(id+"F0.wireOp",EDGE,"E1.filletArc"),sQuery(id+"F0.wireOp",EDGE,"E2.filletArc")])],"isStart":true}),makeQuery(id+"F7.opExtrude","SWEPT_FACE",FACE,{"disambiguationData":[OSD([sQuery(id+"F6.wireOp",EDGE,"E38")])]})]});
            var Q58;
            {var subQ0=sQuery(id+"F6.wireOp",EDGE,"E17");Q58=makeQuery(id+"F7.boolean.opBoolean","INTERSECT",EDGE,{"derivedFrom":[makeQuery(id+"F1.opExtrude","CAP_FACE",FACE,{"disambiguationData":[OSD([sQuery(id+"F0.wireOp",EDGE,"E0.bottom"),sQuery(id+"F0.wireOp",EDGE,"E0.top"),sQuery(id+"F0.wireOp",EDGE,"E0.left"),sQuery(id+"F0.wireOp",EDGE,"E0.right"),sQuery(id+"F0.wireOp",EDGE,"E1.filletArc"),sQuery(id+"F0.wireOp",EDGE,"E2.filletArc")])],"isStart":true}),makeQuery(id+"F7.opExtrude","SWEPT_FACE",FACE,{"disambiguationData":[OSD([subQ0]),TDD([makeQuery(id+"F6.imprint","IMPRINT",EDGE,{"disambiguationData":[TD([[makeQuery(id+"F6.imprint","INTERSECT",VERTEX,{"derivedFrom":[subQ0,sQuery(id+"F6.wireOp",EDGE,"E33")]}),-1.0]])],"derivedFrom":subQ0})])]})]});}
            var Q59;
            Q59=makeQuery(id+"F7.boolean.opBoolean","INTERSECT",EDGE,{"derivedFrom":[makeQuery(id+"F1.opExtrude","CAP_FACE",FACE,{"disambiguationData":[OSD([sQuery(id+"F0.wireOp",EDGE,"E0.bottom"),sQuery(id+"F0.wireOp",EDGE,"E0.top"),sQuery(id+"F0.wireOp",EDGE,"E0.left"),sQuery(id+"F0.wireOp",EDGE,"E0.right"),sQuery(id+"F0.wireOp",EDGE,"E1.filletArc"),sQuery(id+"F0.wireOp",EDGE,"E2.filletArc")])],"isStart":true}),makeQuery(id+"F7.opExtrude","SWEPT_FACE",FACE,{"disambiguationData":[OSD([sQuery(id+"F6.wireOp",EDGE,"E39")])]})]});
            fillet(context, id + "F8", {"entities" : qUnion([Q0, Q1, Q2, Q3, Q4, Q5, Q6, Q7, Q8, Q9, Q10, Q11, Q12, Q13, Q14, Q15, Q16, Q17, Q18, Q19, Q20, Q21, Q22, Q23, Q24, Q25, Q26, Q27, Q28, Q29, Q30, Q31, Q32, Q33, Q34, Q35, Q36, Q37, Q38, Q39, Q40, Q41, Q42, Q43, Q44, Q45, Q46, Q47, Q48, Q49, Q50, Q51, Q52, Q53, Q54, Q55, Q56, Q57, Q58, Q59]), "radius" : 5.08 * mm, "tangentPropagation" : true, "allowEdgeOverflow" : false});
        }
    });
